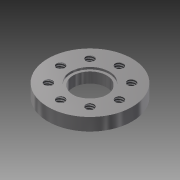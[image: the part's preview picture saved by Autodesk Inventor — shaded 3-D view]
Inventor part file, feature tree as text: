
AUTODESK INVENTOR PART (.ipt)
format: ipt  version: 2013 (Build 170138000, 138)  size: 135,168 bytes
history: native  units: mm
features: sketch x4, extrude x2, hole x2, other x1, pattern_circular x1
ambient origin geometry x1: Origin
feature tree (10):
  other  "ソリッド1"
  extrude  "押し出し1"  Depth=20.0mm
  hole  "穴4"  [1 undecoded]
  hole  "穴5"  [1 undecoded]
  extrude  "押し出し4"  Depth=2.0mm
  pattern_circular  "円形状パターン3"  [2 undecoded]
  sketch  "スケッチ1"
  sketch  "スケッチ2"
  sketch  "スケッチ5"
  sketch  "スケッチ6"
note: 4 required parameter values undecoded (feature->parameter linkage not recoverable at this tier; creation-order binding heuristic only, values carry confidence <= 0.55)
